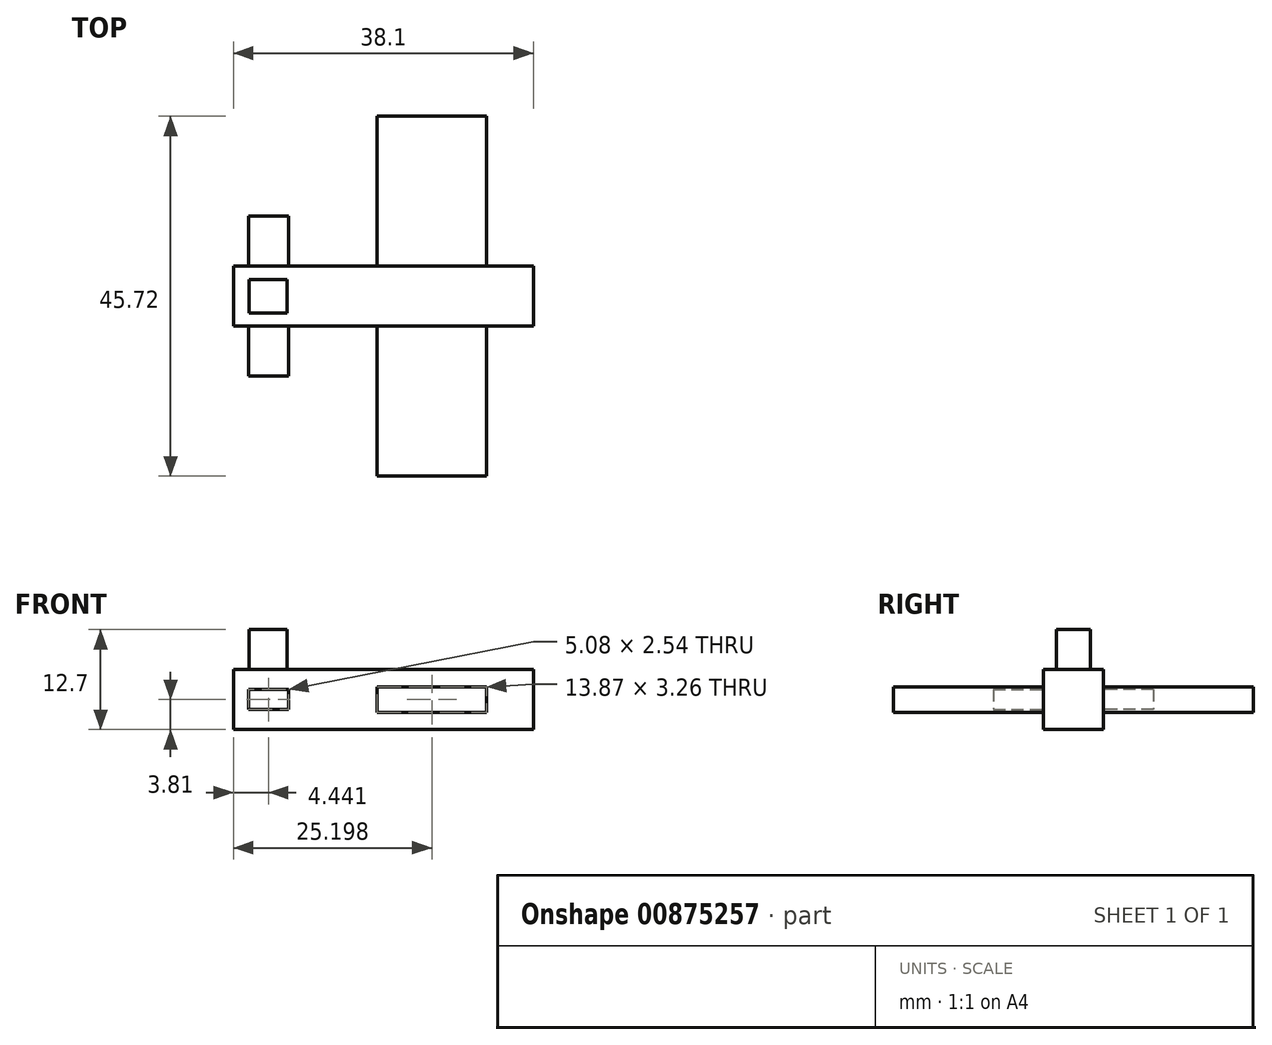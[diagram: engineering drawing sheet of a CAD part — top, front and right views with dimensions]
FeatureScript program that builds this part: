
annotation { "Feature Type Name" : "Feature", "Feature Type Description" : "" }
export const myFeature = defineFeature(function(context is Context, id is Id, definition is map)
    precondition{}
    {
        {
            var Q0;
            Q0=qCreatedBy(makeId("Top.planeOp"),FACE);
            var sketch = newSketch(context, id + "F0", { "sketchPlane" : qUnion([Q0])});
            skLineSegment(sketch, "E0.bottom", {"start": v(-65.76, 4.05) * mm, "end": v(-27.66, 4.05) * mm});
            skLineSegment(sketch, "E0.top", {"start": v(-65.76, 7.86) * mm, "end": v(-27.66, 7.86) * mm});
            skLineSegment(sketch, "E0.left", {"start": v(-65.76, 4.05) * mm, "end": v(-65.76, 7.86) * mm});
            skLineSegment(sketch, "E0.right", {"start": v(-27.66, 4.05) * mm, "end": v(-27.66, 7.86) * mm});
            skSolve(sketch);
        }
        {
            var Q0;
            Q0 = qSketchRegion(id + "F0", true);
            extrude(context, id + "F1", {"entities" : qUnion([Q0]), "depth" : 7.62 * mm, "offsetDistance" : 25.4 * mm});
        }
        {
            var Q0;
            Q0=makeQuery(id+"F1.opExtrude","SWEPT_FACE",FACE,{"disambiguationData":[OSD([sQuery(id+"F0.wireOp",EDGE,"E0.top")])]});
            var sketch = newSketch(context, id + "F2", { "sketchPlane" : qUnion([Q0])});
            skLineSegment(sketch, "E1.bottom", {"start": v(33.63, 5.44) * mm, "end": v(47.5, 5.44) * mm});
            skLineSegment(sketch, "E1.top", {"start": v(33.63, 2.18) * mm, "end": v(47.5, 2.18) * mm});
            skLineSegment(sketch, "E1.left", {"start": v(33.63, 5.44) * mm, "end": v(33.63, 2.18) * mm});
            skLineSegment(sketch, "E1.right", {"start": v(47.5, 5.44) * mm, "end": v(47.5, 2.18) * mm});
            skSolve(sketch);
        }
        {
            var Q0;
            Q0 = qSketchRegion(id + "F2", true);
            extrude(context, id + "F3", {"entities" : qUnion([Q0]), "operationType" : NewBodyOperationType.ADD, "depth" : 19.05 * mm, "offsetDistance" : 25.4 * mm});
        }
        {
            var Q0;
            Q0=makeQuery(id+"F1.opExtrude","SWEPT_FACE",FACE,{"disambiguationData":[OSD([sQuery(id+"F0.wireOp",EDGE,"E0.top")])]});
            var sketch = newSketch(context, id + "F4", { "sketchPlane" : qUnion([Q0])});
            skLineSegment(sketch, "E2.bottom", {"start": v(58.78, 5.08) * mm, "end": v(63.86, 5.08) * mm});
            skLineSegment(sketch, "E2.top", {"start": v(58.78, 2.54) * mm, "end": v(63.86, 2.54) * mm});
            skLineSegment(sketch, "E2.left", {"start": v(58.78, 5.08) * mm, "end": v(58.78, 2.54) * mm});
            skLineSegment(sketch, "E2.right", {"start": v(63.86, 5.08) * mm, "end": v(63.86, 2.54) * mm});
            skSolve(sketch);
        }
        {
            var Q0;
            Q0 = qSketchRegion(id + "F4", true);
            extrude(context, id + "F5", {"entities" : qUnion([Q0]), "operationType" : NewBodyOperationType.ADD, "depth" : 6.35 * mm, "offsetDistance" : 25.4 * mm});
        }
        {
            var Q0;
            Q0=makeQuery(id+"F1.opExtrude","CAP_FACE",FACE,{"disambiguationData":[OSD([sQuery(id+"F0.wireOp",EDGE,"E0.bottom"),sQuery(id+"F0.wireOp",EDGE,"E0.top"),sQuery(id+"F0.wireOp",EDGE,"E0.left"),sQuery(id+"F0.wireOp",EDGE,"E0.right")])],"isStart":false});
            var sketch = newSketch(context, id + "F6", { "sketchPlane" : qUnion([Q0])});
            skLineSegment(sketch, "E3.bottom", {"start": v(-63.75, 4.05) * mm, "end": v(-58.96, 4.05) * mm});
            skLineSegment(sketch, "E3.top", {"start": v(-63.75, 6.19) * mm, "end": v(-58.96, 6.19) * mm});
            skLineSegment(sketch, "E3.left", {"start": v(-63.75, 4.05) * mm, "end": v(-63.75, 6.19) * mm});
            skLineSegment(sketch, "E3.right", {"start": v(-58.96, 4.05) * mm, "end": v(-58.96, 6.19) * mm});
            skSolve(sketch);
        }
        {
            var Q0;
            Q0 = qSketchRegion(id + "F6", true);
            extrude(context, id + "F7", {"entities" : qUnion([Q0]), "operationType" : NewBodyOperationType.ADD, "depth" : 5.08 * mm, "offsetDistance" : 25.4 * mm});
        }
        {
            var Q0;
            Q0=makeQuery(id+"F1.opExtrude","SWEPT_BODY",BODY,{"disambiguationData":[OSD([sQuery(id+"F0.wireOp",EDGE,"E0.bottom"),sQuery(id+"F0.wireOp",EDGE,"E0.top"),sQuery(id+"F0.wireOp",EDGE,"E0.left"),sQuery(id+"F0.wireOp",EDGE,"E0.right")])]});
            var Q1;
            Q1=makeQuery(id+"F7.boolean.opBoolean","MERGE",FACE,{"derivedFrom":[makeQuery(id+"F1.opExtrude","SWEPT_FACE",FACE,{"disambiguationData":[OSD([sQuery(id+"F0.wireOp",EDGE,"E0.bottom")])]}),makeQuery(id+"F7.opExtrude","SWEPT_FACE",FACE,{"disambiguationData":[OSD([sQuery(id+"F6.wireOp",EDGE,"E3.bottom")])]})]});
            mirror(context, id + "F8", {"operationType" : NewBodyOperationType.ADD, "entities" : qUnion([Q0]), "mirrorPlane" : qUnion([Q1])});
        }
    });
